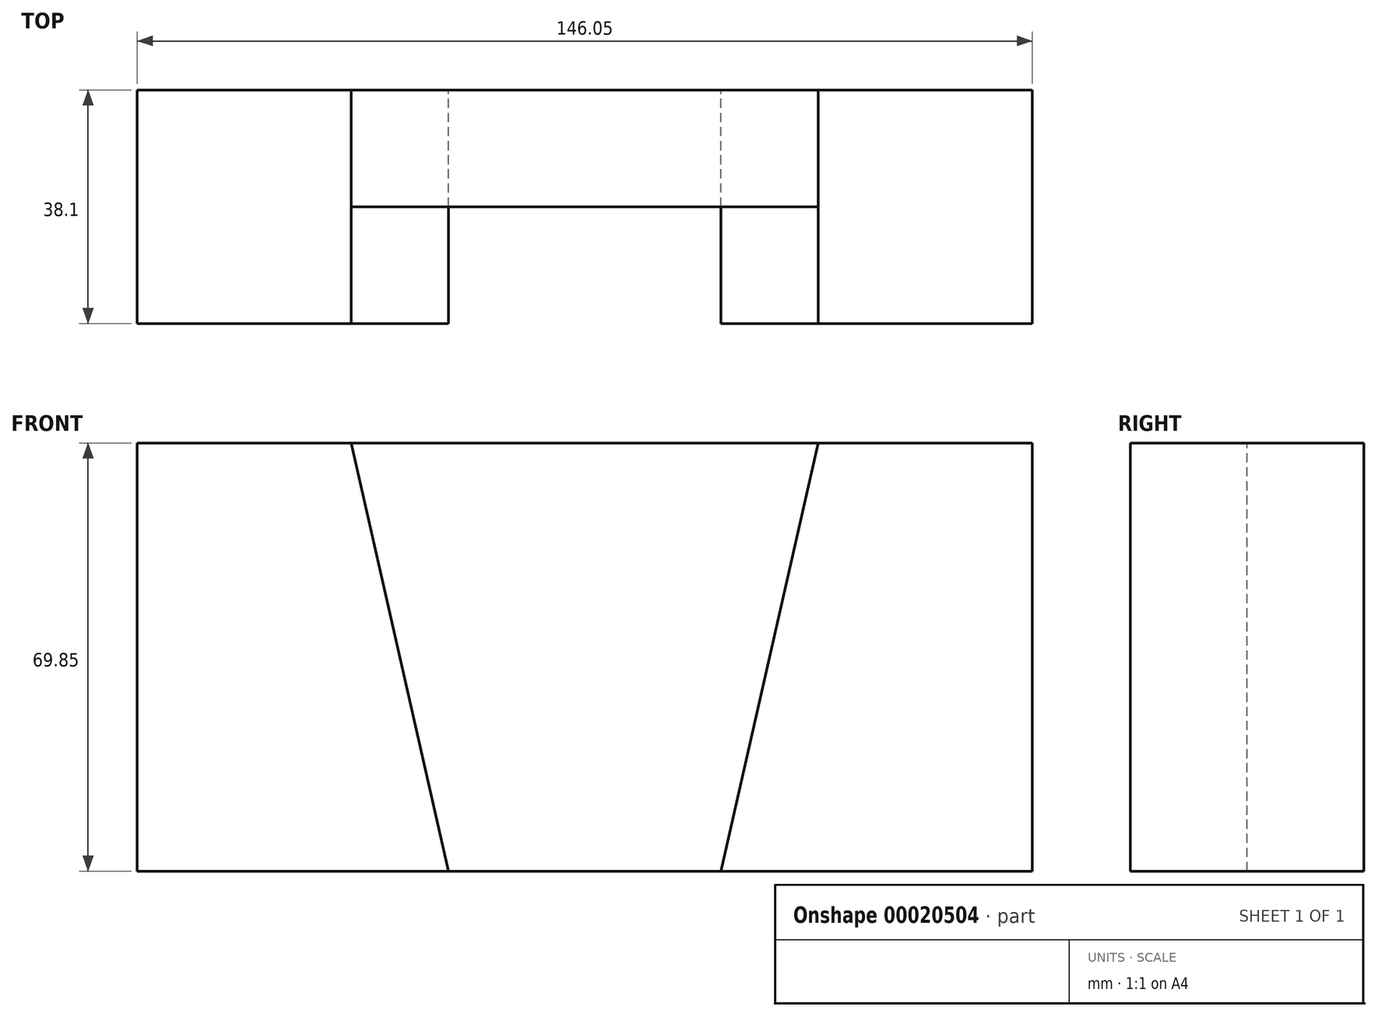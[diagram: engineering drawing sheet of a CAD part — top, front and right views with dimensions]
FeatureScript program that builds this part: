
annotation { "Feature Type Name" : "Feature", "Feature Type Description" : "" }
export const myFeature = defineFeature(function(context is Context, id is Id, definition is map)
    precondition{}
    {
        {
            var Q0;
            Q0=qCreatedBy(makeId("Front.planeOp"),FACE);
            var sketch = newSketch(context, id + "F0", { "sketchPlane" : qUnion([Q0])});
            skLineSegment(sketch, "E0", {"start": v(-40.12, 49.06) * mm, "end": v(36.08, 49.06) * mm});
            skLineSegment(sketch, "E1", {"start": v(36.08, 49.06) * mm, "end": v(20.2, -20.8) * mm});
            skLineSegment(sketch, "E2", {"start": v(20.2, -20.8) * mm, "end": v(-24.24, -20.8) * mm});
            skLineSegment(sketch, "E3", {"start": v(-24.24, -20.8) * mm, "end": v(-40.12, 49.06) * mm});
            skLineSegment(sketch, "E4", {"start": v(-40.12, 49.06) * mm, "end": v(-75.04, 49.06) * mm});
            skLineSegment(sketch, "E5", {"start": v(-75.04, 49.06) * mm, "end": v(-75.04, -20.8) * mm});
            skLineSegment(sketch, "E6", {"start": v(-75.04, -20.8) * mm, "end": v(-24.24, -20.8) * mm});
            skLineSegment(sketch, "E7", {"start": v(36.08, 49.06) * mm, "end": v(71, 49.06) * mm});
            skLineSegment(sketch, "E8", {"start": v(71, 49.06) * mm, "end": v(71, -20.8) * mm});
            skLineSegment(sketch, "E9", {"start": v(71, -20.8) * mm, "end": v(20.2, -20.8) * mm});
            skSolve(sketch);
        }
        {
            var Q0;
            Q0=makeQuery(id+"F0.imprint","IMPRINT",FACE,{"disambiguationData":[TD([[makeQuery(id+"F0.imprint","IMPRINT",EDGE,{"derivedFrom":sQuery(id+"F0.wireOp",EDGE,"E3")}),1.0]])]});
            var Q1;
            Q1=makeQuery(id+"F0.imprint","IMPRINT",FACE,{"disambiguationData":[TD([[makeQuery(id+"F0.imprint","IMPRINT",EDGE,{"derivedFrom":sQuery(id+"F0.wireOp",EDGE,"E1")}),1.0]])]});
            extrude(context, id + "F1", {"entities" : qUnion([Q0, Q1]), "depth" : 38.1 * mm});
        }
        {
            var Q0;
            Q0=makeQuery(id+"F0.imprint","IMPRINT",FACE,{"disambiguationData":[TD([[makeQuery(id+"F0.imprint","IMPRINT",EDGE,{"derivedFrom":sQuery(id+"F0.wireOp",EDGE,"E0")}),-1.0]])]});
            extrude(context, id + "F2", {"entities" : qUnion([Q0]), "depth" : 19.05 * mm});
        }
    });
